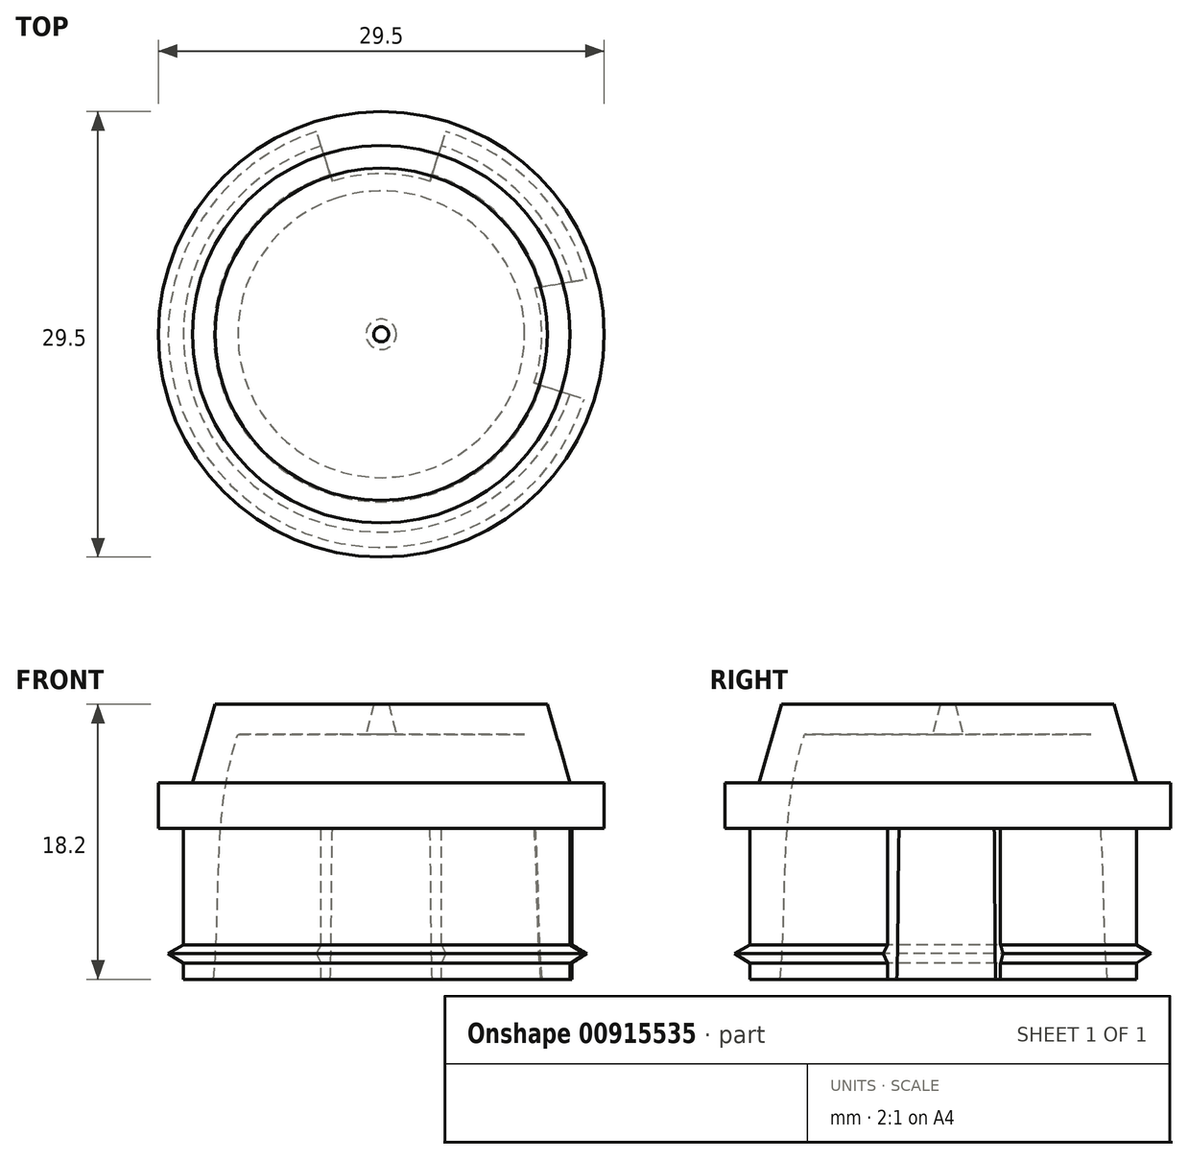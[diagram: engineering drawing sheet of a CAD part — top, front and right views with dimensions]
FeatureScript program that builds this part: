
annotation { "Feature Type Name" : "Feature", "Feature Type Description" : "" }
export const myFeature = defineFeature(function(context is Context, id is Id, definition is map)
    precondition{}
    {
        {
            var Q0;
            Q0=qCreatedBy(makeId("Front.planeOp"),FACE);
            var sketch = newSketch(context, id + "F0", { "sketchPlane" : qUnion([Q0])});
            skPoint(sketch, "E0.middle", {"position": v(0, 0) * mm});
            skLineSegment(sketch, "E1", {"start": v(-11, 6.7) * mm, "end": v(-0.5, 6.7) * mm});
            skLineSegment(sketch, "E2", {"start": v(-11, 6.7) * mm, "end": v(-12.5, 1.5) * mm});
            skLineSegment(sketch, "E3", {"start": v(-12.5, 1.5) * mm, "end": v(-14.75, 1.5) * mm});
            skLineSegment(sketch, "E4", {"start": v(-14.75, -1.5) * mm, "end": v(-13.1, -1.5) * mm});
            skLineSegment(sketch, "E5", {"start": v(-14.75, 1.5) * mm, "end": v(-14.75, -1.5) * mm});
            skLineSegment(sketch, "E6", {"start": v(0, 18.2) * mm, "end": v(0, 6.7) * mm, "construction": true});
            skLineSegment(sketch, "E7", {"start": v(11.53, 0) * mm, "end": v(-24.4, 0) * mm, "construction": true});
            skLineSegment(sketch, "E8", {"start": v(-13.1, -11.5) * mm, "end": v(-11.1, -11.5) * mm});
            skFitSpline(sketch, "E9", {"points": [v(-11.1, -11.5) * mm, v(-9.49, 4.7) * mm], "startDerivative": vector(1.61, 16.2) * mm, "endDerivative": vector(5.16, 15.76) * mm});
            skLineSegment(sketch, "E10", {"start": v(-9.49, 4.7) * mm, "end": v(-1, 4.7) * mm});
            skLineSegment(sketch, "E11", {"start": v(0, 6.7) * mm, "end": v(0, 4.7) * mm});
            skLineSegment(sketch, "E12", {"start": v(-14.1, -9.8) * mm, "end": v(-13.1, -10.43) * mm});
            skLineSegment(sketch, "E13", {"start": v(-14.1, -9.8) * mm, "end": v(-13.1, -9.21) * mm});
            skLineSegment(sketch, "E14", {"start": v(-13.1, -10.43) * mm, "end": v(-13.1, -11.5) * mm});
            skLineSegment(sketch, "E15", {"start": v(-13.1, -9.21) * mm, "end": v(-13.1, -1.5) * mm});
            skLineSegment(sketch, "E16", {"start": v(-0.5, 6.7) * mm, "end": v(-1, 4.7) * mm});
            skPoint(sketch, "E17.orphan", {"position": v(-0.5, 6.25) * mm});
            skPoint(sketch, "E18.end.orphan", {"position": v(-0.5, 7.02) * mm});
            skLineSegment(sketch, "E19.trimOffspring", {"start": v(0, 4.7) * mm, "end": v(0, -19.41) * mm, "construction": true});
            skSolve(sketch);
        }
        {
            var Q0;
            Q0=makeQuery(id+"F0.imprint","IMPRINT",FACE,{"disambiguationData":[TD([[makeQuery(id+"F0.imprint","IMPRINT",EDGE,{"derivedFrom":sQuery(id+"F0.wireOp",EDGE,"E1")}),-1.0]])]});
            var Q1;
            Q1=sQuery(id+"F0.wireOp",EDGE,"E6");
            revolve(context, id + "F1", {"surfaceOperationType" : NewSurfaceOperationType.NEW, "entities" : qUnion([Q0]), "axis" : qUnion([Q1]), "revolveType" : RevolveType.FULL});
        }
        {
            var Q0;
            Q0=makeQuery(id+"F1.opRevolve","SWEPT_FACE",FACE,{"disambiguationData":[OSD([sQuery(id+"F0.wireOp",EDGE,"E8")])]});
            cPlane(context, id + "F2", {"entities" : qUnion([Q0]), "cplaneType" : CPlaneType.OFFSET, "offset" : 0 * mm, "width" : 150 * mm, "height" : 150 * mm});
        }
        {
            var Q0;
            Q0=qCreatedBy(id+"F2.planeOp",FACE);
            var sketch = newSketch(context, id + "F3", { "sketchPlane" : qUnion([Q0])});
            skLineSegment(sketch, "E20", {"start": v(0, 18) * mm, "end": v(0, -20.04) * mm, "construction": true});
            skLineSegment(sketch, "E21", {"start": v(-19.2, 0) * mm, "end": v(26.1, 0) * mm, "construction": true});
            skLineSegment(sketch, "E22", {"start": v(4, 12.54) * mm, "end": v(-4, 12.54) * mm, "construction": true});
            skLineSegment(sketch, "E23", {"start": v(0, 0) * mm, "end": v(-19.8, 6.31) * mm, "construction": true});
            skLineSegment(sketch, "E24", {"start": v(-13.62, 4.34) * mm, "end": v(-13.62, -3.66) * mm, "construction": true});
            skLineSegment(sketch, "E25", {"start": v(0, 0) * mm, "end": v(-17.87, -5.7) * mm, "construction": true});
            skArc(sketch, "E26", {"start": v(-13.62, -3.66) * mm, "mid": v(-14.1, 0.33) * mm, "end": v(-13.43, 4.28) * mm});
            skArc(sketch, "E27", {"start": v(-2.88, 9.04) * mm, "mid": v(0, 9.49) * mm, "end": v(2.88, 9.04) * mm});
            skArc(sketch, "E28", {"start": v(-9.04, -2.88) * mm, "mid": v(-9.49, 0) * mm, "end": v(-9.04, 2.88) * mm});
            skLineSegment(sketch, "E29", {"start": v(2.88, 9.04) * mm, "end": v(4.3, 13.48) * mm});
            skLineSegment(sketch, "E30", {"start": v(-4.3, 13.48) * mm, "end": v(-2.88, 9.04) * mm});
            skLineSegment(sketch, "E31", {"start": v(-9.04, 2.88) * mm, "end": v(-13.62, 4.34) * mm});
            skArc(sketch, "E32.MirrorCS", {"start": v(-2.88, -9.04) * mm, "mid": v(0, -9.49) * mm, "end": v(2.88, -9.04) * mm});
            skArc(sketch, "E33.MirrorCS", {"start": v(13.62, -3.66) * mm, "mid": v(14.1, 0.33) * mm, "end": v(13.43, 4.28) * mm});
            skArc(sketch, "E34.MirrorCS", {"start": v(9.04, -2.88) * mm, "mid": v(9.49, 0) * mm, "end": v(9.04, 2.88) * mm});
            skLineSegment(sketch, "E35", {"start": v(0, 0) * mm, "end": v(-4.28, -13.42) * mm, "construction": true});
            skLineSegment(sketch, "E36", {"start": v(0, 0) * mm, "end": v(4.1, -12.85) * mm, "construction": true});
            skArc(sketch, "E37", {"start": v(4.28, -13.43) * mm, "mid": v(0, -14.1) * mm, "end": v(-4.28, -13.43) * mm});
            skLineSegment(sketch, "E38", {"start": v(-2.88, -9.04) * mm, "end": v(-4.28, -13.43) * mm});
            skLineSegment(sketch, "E39", {"start": v(2.88, -9.04) * mm, "end": v(4.28, -13.43) * mm});
            skLineSegment(sketch, "E40", {"start": v(9.04, -2.88) * mm, "end": v(13.62, -3.66) * mm});
            skLineSegment(sketch, "E41", {"start": v(9.04, 2.88) * mm, "end": v(13.43, 4.28) * mm});
            skLineSegment(sketch, "E42", {"start": v(-9.04, -2.88) * mm, "end": v(-13.62, -3.66) * mm});
            skLineSegment(sketch, "E43", {"start": v(-13.43, 4.28) * mm, "end": v(-9.04, 2.88) * mm});
            skArc(sketch, "E44", {"start": v(-4.3, 13.48) * mm, "mid": v(0, 14.15) * mm, "end": v(4.3, 13.48) * mm});
            skSolve(sketch);
        }
        {
            var Q0;
            Q0=makeQuery(id+"F3.imprint","IMPRINT",FACE,{"disambiguationData":[TD([[makeQuery(id+"F3.imprint","IMPRINT",EDGE,{"derivedFrom":sQuery(id+"F3.wireOp",EDGE,"E27")}),1.0]])]});
            var Q1;
            Q1=makeQuery(id+"F3.imprint","IMPRINT",FACE,{"disambiguationData":[TD([[makeQuery(id+"F3.imprint","IMPRINT",EDGE,{"derivedFrom":sQuery(id+"F3.wireOp",EDGE,"E33.MirrorCS")}),1.0]])]});
            var Q2;
            Q2=makeQuery(id+"F3.imprint","IMPRINT",FACE,{"disambiguationData":[TD([[makeQuery(id+"F3.imprint","IMPRINT",EDGE,{"derivedFrom":sQuery(id+"F3.wireOp",EDGE,"E32.MirrorCS")}),-1.0]])]});
            var Q3;
            {var subQ0=sQuery(id+"F3.wireOp",EDGE,"E26");Q3=makeQuery(id+"F3.imprint","IMPRINT",FACE,{"disambiguationData":[TD([[makeQuery(id+"F3.imprint","IMPRINT",EDGE,{"derivedFrom":subQ0}),-1.0]])]});}
            extrude(context, id + "F4", {"entities" : qUnion([Q0, Q1, Q2, Q3]), "operationType" : NewBodyOperationType.REMOVE, "oppositeDirection" : true, "depth" : 10 * mm, "offsetDistance" : 25 * mm});
        }
    });
